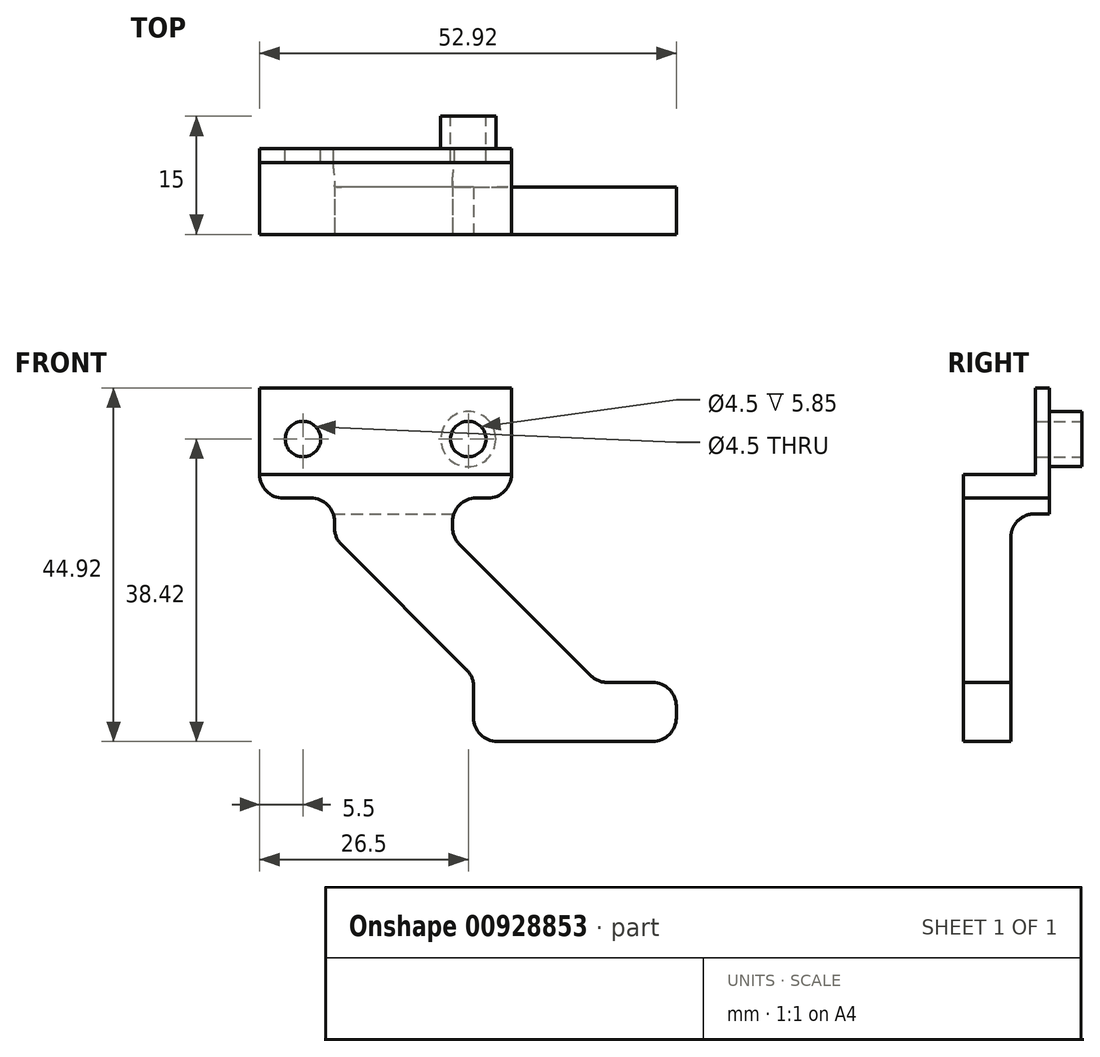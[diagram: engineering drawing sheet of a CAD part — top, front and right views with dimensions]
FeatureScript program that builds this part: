
annotation { "Feature Type Name" : "Feature", "Feature Type Description" : "" }
export const myFeature = defineFeature(function(context is Context, id is Id, definition is map)
    precondition{}
    {
        {
            var Q0;
            Q0=qCreatedBy(makeId("Front.planeOp"),FACE);
            var sketch = newSketch(context, id + "F0", { "sketchPlane" : qUnion([Q0])});
            skLineSegment(sketch, "E0", {"start": v(0, 0) * mm, "end": v(32, 0) * mm});
            skLineSegment(sketch, "E1", {"start": v(32, 0) * mm, "end": v(32, -11) * mm});
            skLineSegment(sketch, "E2", {"start": v(29, -14) * mm, "end": v(27.5, -14) * mm});
            skLineSegment(sketch, "E3", {"start": v(24.5, -17) * mm, "end": v(24.5, -17.76) * mm});
            skLineSegment(sketch, "E4", {"start": v(25.38, -19.88) * mm, "end": v(42.04, -36.54) * mm});
            skLineSegment(sketch, "E5", {"start": v(26.3, -35.8) * mm, "end": v(10.38, -19.88) * mm});
            skLineSegment(sketch, "E6", {"start": v(9.5, -17.76) * mm, "end": v(9.5, -17) * mm});
            skLineSegment(sketch, "E7", {"start": v(6.5, -14) * mm, "end": v(3, -14) * mm});
            skLineSegment(sketch, "E8", {"start": v(0, -11) * mm, "end": v(0, 0) * mm});
            skLineSegment(sketch, "E9", {"start": v(44.16, -37.42) * mm, "end": v(49.92, -37.42) * mm});
            skLineSegment(sketch, "E10", {"start": v(52.92, -40.42) * mm, "end": v(52.92, -41.92) * mm});
            skLineSegment(sketch, "E11", {"start": v(49.92, -44.92) * mm, "end": v(30.18, -44.92) * mm});
            skLineSegment(sketch, "E12", {"start": v(27.18, -41.92) * mm, "end": v(27.18, -37.92) * mm});
            skPoint(sketch, "E13.visualSharp", {"position": v(32, -14) * mm});
            skArc(sketch, "E13.filletArc", {"start": v(29, -14) * mm, "mid": v(31.12, -13.12) * mm, "end": v(32, -11) * mm});
            skPoint(sketch, "E14.visualSharp", {"position": v(24.5, -14) * mm});
            skArc(sketch, "E14.filletArc", {"start": v(27.5, -14) * mm, "mid": v(25.38, -14.88) * mm, "end": v(24.5, -17) * mm});
            skPoint(sketch, "E15.visualSharp", {"position": v(24.5, -19) * mm});
            skArc(sketch, "E15.filletArc", {"start": v(24.5, -17.76) * mm, "mid": v(24.73, -18.9) * mm, "end": v(25.38, -19.88) * mm});
            skPoint(sketch, "E16.visualSharp", {"position": v(42.92, -37.42) * mm});
            skArc(sketch, "E16.filletArc", {"start": v(42.04, -36.54) * mm, "mid": v(43.01, -37.2) * mm, "end": v(44.16, -37.42) * mm});
            skPoint(sketch, "E17.visualSharp", {"position": v(52.92, -37.42) * mm});
            skArc(sketch, "E17.filletArc", {"start": v(52.92, -40.42) * mm, "mid": v(52.04, -38.3) * mm, "end": v(49.92, -37.42) * mm});
            skPoint(sketch, "E18.visualSharp", {"position": v(52.92, -44.92) * mm});
            skArc(sketch, "E18.filletArc", {"start": v(49.92, -44.92) * mm, "mid": v(52.04, -44.04) * mm, "end": v(52.92, -41.92) * mm});
            skPoint(sketch, "E19.visualSharp", {"position": v(27.18, -44.92) * mm});
            skArc(sketch, "E19.filletArc", {"start": v(27.18, -41.92) * mm, "mid": v(28.06, -44.04) * mm, "end": v(30.18, -44.92) * mm});
            skPoint(sketch, "E20.visualSharp", {"position": v(27.18, -36.68) * mm});
            skArc(sketch, "E20.filletArc", {"start": v(27.18, -37.92) * mm, "mid": v(26.95, -36.77) * mm, "end": v(26.3, -35.8) * mm});
            skPoint(sketch, "E21.visualSharp", {"position": v(9.5, -19) * mm});
            skArc(sketch, "E21.filletArc", {"start": v(9.5, -17.76) * mm, "mid": v(9.73, -18.9) * mm, "end": v(10.38, -19.88) * mm});
            skPoint(sketch, "E22.visualSharp", {"position": v(9.5, -14) * mm});
            skArc(sketch, "E22.filletArc", {"start": v(9.5, -17) * mm, "mid": v(8.62, -14.88) * mm, "end": v(6.5, -14) * mm});
            skPoint(sketch, "E23.visualSharp", {"position": v(0, -14) * mm});
            skArc(sketch, "E23.filletArc", {"start": v(0, -11) * mm, "mid": v(0.88, -13.12) * mm, "end": v(3, -14) * mm});
            skSolve(sketch);
        }
        {
            var Q0;
            Q0=qSketchRegion(id+"F0",true);
            extrude(context, id + "F1", {"entities" : qUnion([Q0]), "depth" : 15 * mm, "offsetDistance" : 25 * mm});
        }
        {
            var Q0;
            Q0=makeQuery(id+"F1.opExtrude","CAP_FACE",FACE,{"disambiguationData":[OSD([sQuery(id+"F0.wireOp",EDGE,"E0"),sQuery(id+"F0.wireOp",EDGE,"E1"),sQuery(id+"F0.wireOp",EDGE,"E2"),sQuery(id+"F0.wireOp",EDGE,"E3"),sQuery(id+"F0.wireOp",EDGE,"E4"),sQuery(id+"F0.wireOp",EDGE,"E5"),sQuery(id+"F0.wireOp",EDGE,"E6"),sQuery(id+"F0.wireOp",EDGE,"E7"),sQuery(id+"F0.wireOp",EDGE,"E8"),sQuery(id+"F0.wireOp",EDGE,"E9"),sQuery(id+"F0.wireOp",EDGE,"E10"),sQuery(id+"F0.wireOp",EDGE,"E11"),sQuery(id+"F0.wireOp",EDGE,"E12"),sQuery(id+"F0.wireOp",EDGE,"E13.filletArc"),sQuery(id+"F0.wireOp",EDGE,"E14.filletArc"),sQuery(id+"F0.wireOp",EDGE,"E15.filletArc"),sQuery(id+"F0.wireOp",EDGE,"E16.filletArc"),sQuery(id+"F0.wireOp",EDGE,"E17.filletArc"),sQuery(id+"F0.wireOp",EDGE,"E18.filletArc"),sQuery(id+"F0.wireOp",EDGE,"E19.filletArc"),sQuery(id+"F0.wireOp",EDGE,"E20.filletArc"),sQuery(id+"F0.wireOp",EDGE,"E21.filletArc"),sQuery(id+"F0.wireOp",EDGE,"E22.filletArc"),sQuery(id+"F0.wireOp",EDGE,"E23.filletArc")])],"isStart":false});
            var sketch = newSketch(context, id + "F2", { "sketchPlane" : qUnion([Q0])});
            skLineSegment(sketch, "E24", {"start": v(0, 0) * mm, "end": v(32, 0) * mm, "construction": true});
            skLineSegment(sketch, "E25", {"start": v(32, 0) * mm, "end": v(32, -14) * mm, "construction": true});
            skLineSegment(sketch, "E26", {"start": v(32, -14) * mm, "end": v(0, -14) * mm, "construction": true});
            skLineSegment(sketch, "E27", {"start": v(0, -14) * mm, "end": v(0, 0) * mm, "construction": true});
            skLineSegment(sketch, "E28", {"start": v(0, -6.5) * mm, "end": v(32, -6.5) * mm, "construction": true});
            skCircle(sketch, "E29", {"center": v(5.5, -6.5) * mm, "radius": 3.5 * mm});
            skLineSegment(sketch, "E30", {"start": v(16, 0) * mm, "end": v(16, -14) * mm, "construction": true});
            skCircle(sketch, "E31.MirrorC", {"center": v(26.5, -6.5) * mm, "radius": 3.5 * mm});
            skSolve(sketch);
        }
        {
            var Q0;
            Q0=makeQuery(id+"F2.imprint","IMPRINT",FACE,{"disambiguationData":[TD([[makeQuery(id+"F2.imprint","IMPRINT",EDGE,{"derivedFrom":sQuery(id+"F2.wireOp",EDGE,"E31.MirrorC")}),-1.0]])]});
            var Q1;
            Q1=makeQuery(id+"F2.imprint","IMPRINT",FACE,{"disambiguationData":[TD([[makeQuery(id+"F2.imprint","IMPRINT",EDGE,{"derivedFrom":sQuery(id+"F2.wireOp",EDGE,"E29")}),1.0]])]});
            extrude(context, id + "F3", {"entities" : qUnion([Q0, Q1]), "operationType" : NewBodyOperationType.REMOVE, "oppositeDirection" : true, "depth" : 4.1 * mm, "offsetDistance" : 25 * mm});
        }
        {
            var Q0;
            Q0=makeQuery(id+"F1.opExtrude","CAP_FACE",FACE,{"disambiguationData":[OSD([sQuery(id+"F0.wireOp",EDGE,"E0"),sQuery(id+"F0.wireOp",EDGE,"E1"),sQuery(id+"F0.wireOp",EDGE,"E2"),sQuery(id+"F0.wireOp",EDGE,"E3"),sQuery(id+"F0.wireOp",EDGE,"E4"),sQuery(id+"F0.wireOp",EDGE,"E5"),sQuery(id+"F0.wireOp",EDGE,"E6"),sQuery(id+"F0.wireOp",EDGE,"E7"),sQuery(id+"F0.wireOp",EDGE,"E8"),sQuery(id+"F0.wireOp",EDGE,"E9"),sQuery(id+"F0.wireOp",EDGE,"E10"),sQuery(id+"F0.wireOp",EDGE,"E11"),sQuery(id+"F0.wireOp",EDGE,"E12"),sQuery(id+"F0.wireOp",EDGE,"E13.filletArc"),sQuery(id+"F0.wireOp",EDGE,"E14.filletArc"),sQuery(id+"F0.wireOp",EDGE,"E15.filletArc"),sQuery(id+"F0.wireOp",EDGE,"E16.filletArc"),sQuery(id+"F0.wireOp",EDGE,"E17.filletArc"),sQuery(id+"F0.wireOp",EDGE,"E18.filletArc"),sQuery(id+"F0.wireOp",EDGE,"E19.filletArc"),sQuery(id+"F0.wireOp",EDGE,"E20.filletArc"),sQuery(id+"F0.wireOp",EDGE,"E21.filletArc"),sQuery(id+"F0.wireOp",EDGE,"E22.filletArc"),sQuery(id+"F0.wireOp",EDGE,"E23.filletArc")])],"isStart":false});
            var sketch = newSketch(context, id + "F4", { "sketchPlane" : qUnion([Q0])});
            skCircle(sketch, "E32", {"center": v(5.5, -6.5) * mm, "radius": 2.25 * mm});
            skCircle(sketch, "E33", {"center": v(26.5, -6.5) * mm, "radius": 2.25 * mm});
            skSolve(sketch);
        }
        {
            var Q0;
            Q0=qSketchRegion(id+"F4",true);
            extrude(context, id + "F5", {"entities" : qUnion([Q0]), "operationType" : NewBodyOperationType.REMOVE, "oppositeDirection" : true, "depth" : 25 * mm, "offsetDistance" : 25 * mm});
        }
        {
            var Q0;
            Q0=makeQuery(id+"F1.opExtrude","SWEPT_FACE",FACE,{"disambiguationData":[OSD([sQuery(id+"F0.wireOp",EDGE,"E8")])]});
            var sketch = newSketch(context, id + "F6", { "sketchPlane" : qUnion([Q0])});
            skLineSegment(sketch, "E34.bottom", {"start": v(0, 0) * mm, "end": v(9.15, 0) * mm});
            skLineSegment(sketch, "E34.top", {"start": v(0, -11) * mm, "end": v(9.15, -11) * mm});
            skLineSegment(sketch, "E34.left", {"start": v(0, 0) * mm, "end": v(0, -11) * mm});
            skLineSegment(sketch, "E34.right", {"start": v(9.15, 0) * mm, "end": v(9.15, -11) * mm});
            skLineSegment(sketch, "E35.bottom", {"start": v(9, -48) * mm, "end": v(15, -48) * mm});
            skLineSegment(sketch, "E35.top", {"start": v(9, -16) * mm, "end": v(15, -16) * mm});
            skLineSegment(sketch, "E35.left", {"start": v(6, -45) * mm, "end": v(6, -19) * mm});
            skLineSegment(sketch, "E35.right", {"start": v(15, -48) * mm, "end": v(15, -16) * mm});
            skPoint(sketch, "E36.visualSharp", {"position": v(6, -16) * mm});
            skArc(sketch, "E36.filletArc", {"start": v(9, -16) * mm, "mid": v(6.88, -16.88) * mm, "end": v(6, -19) * mm});
            skPoint(sketch, "E37.visualSharp", {"position": v(6, -48) * mm});
            skArc(sketch, "E37.filletArc", {"start": v(6, -45) * mm, "mid": v(6.88, -47.12) * mm, "end": v(9, -48) * mm});
            skSolve(sketch);
        }
        {
            var Q0;
            Q0=qSketchRegion(id+"F6",true);
            extrude(context, id + "F7", {"entities" : qUnion([Q0]), "operationType" : NewBodyOperationType.REMOVE, "endBound" : BoundingType.THROUGH_ALL, "oppositeDirection" : true, "depth" : 25 * mm, "offsetDistance" : 25 * mm});
        }
        {
            var Q0;
            Q0=makeQuery(id+"F1.opExtrude","SWEPT_BODY",BODY,{"disambiguationData":[OSD([sQuery(id+"F0.wireOp",EDGE,"E0"),sQuery(id+"F0.wireOp",EDGE,"E1"),sQuery(id+"F0.wireOp",EDGE,"E2"),sQuery(id+"F0.wireOp",EDGE,"E3"),sQuery(id+"F0.wireOp",EDGE,"E4"),sQuery(id+"F0.wireOp",EDGE,"E5"),sQuery(id+"F0.wireOp",EDGE,"E6"),sQuery(id+"F0.wireOp",EDGE,"E7"),sQuery(id+"F0.wireOp",EDGE,"E8"),sQuery(id+"F0.wireOp",EDGE,"E9"),sQuery(id+"F0.wireOp",EDGE,"E10"),sQuery(id+"F0.wireOp",EDGE,"E11"),sQuery(id+"F0.wireOp",EDGE,"E12"),sQuery(id+"F0.wireOp",EDGE,"E13.filletArc"),sQuery(id+"F0.wireOp",EDGE,"E14.filletArc"),sQuery(id+"F0.wireOp",EDGE,"E15.filletArc"),sQuery(id+"F0.wireOp",EDGE,"E16.filletArc"),sQuery(id+"F0.wireOp",EDGE,"E17.filletArc"),sQuery(id+"F0.wireOp",EDGE,"E18.filletArc"),sQuery(id+"F0.wireOp",EDGE,"E19.filletArc"),sQuery(id+"F0.wireOp",EDGE,"E20.filletArc"),sQuery(id+"F0.wireOp",EDGE,"E21.filletArc"),sQuery(id+"F0.wireOp",EDGE,"E22.filletArc"),sQuery(id+"F0.wireOp",EDGE,"E23.filletArc")])]});
            var Q1;
            Q1=qCreatedBy(makeId("Front.planeOp"),FACE);
            mirror(context, id + "F8", {"entities" : qUnion([Q0]), "mirrorPlane" : qUnion([Q1])});
        }
        {
            var Q0;
            Q0=makeQuery(id+"F1.opExtrude","SWEPT_BODY",BODY,{"disambiguationData":[OSD([sQuery(id+"F0.wireOp",EDGE,"E0"),sQuery(id+"F0.wireOp",EDGE,"E1"),sQuery(id+"F0.wireOp",EDGE,"E2"),sQuery(id+"F0.wireOp",EDGE,"E3"),sQuery(id+"F0.wireOp",EDGE,"E4"),sQuery(id+"F0.wireOp",EDGE,"E5"),sQuery(id+"F0.wireOp",EDGE,"E6"),sQuery(id+"F0.wireOp",EDGE,"E7"),sQuery(id+"F0.wireOp",EDGE,"E8"),sQuery(id+"F0.wireOp",EDGE,"E9"),sQuery(id+"F0.wireOp",EDGE,"E10"),sQuery(id+"F0.wireOp",EDGE,"E11"),sQuery(id+"F0.wireOp",EDGE,"E12"),sQuery(id+"F0.wireOp",EDGE,"E13.filletArc"),sQuery(id+"F0.wireOp",EDGE,"E14.filletArc"),sQuery(id+"F0.wireOp",EDGE,"E15.filletArc"),sQuery(id+"F0.wireOp",EDGE,"E16.filletArc"),sQuery(id+"F0.wireOp",EDGE,"E17.filletArc"),sQuery(id+"F0.wireOp",EDGE,"E18.filletArc"),sQuery(id+"F0.wireOp",EDGE,"E19.filletArc"),sQuery(id+"F0.wireOp",EDGE,"E20.filletArc"),sQuery(id+"F0.wireOp",EDGE,"E21.filletArc"),sQuery(id+"F0.wireOp",EDGE,"E22.filletArc"),sQuery(id+"F0.wireOp",EDGE,"E23.filletArc")])]});
            deleteBodies(context, id + "F9", {"entities" : qUnion([Q0])});
        }
    });
